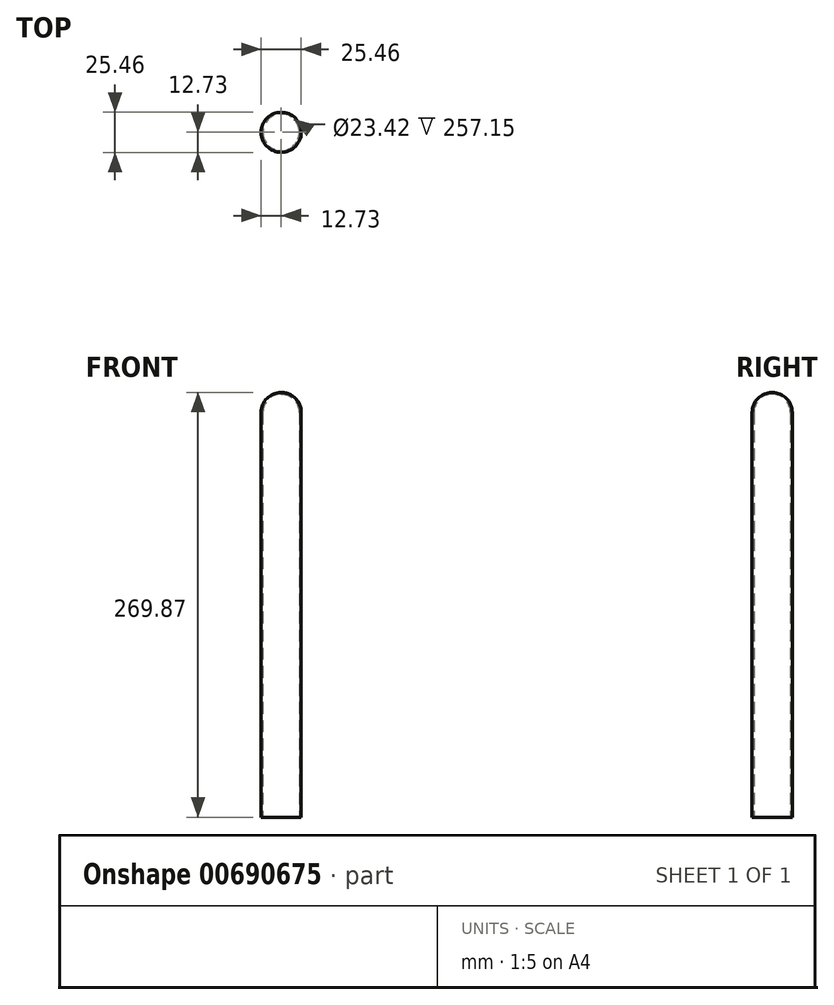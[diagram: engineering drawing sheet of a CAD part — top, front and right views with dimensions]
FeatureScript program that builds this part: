
annotation { "Feature Type Name" : "Feature", "Feature Type Description" : "" }
export const myFeature = defineFeature(function(context is Context, id is Id, definition is map)
    precondition{}
    {
        {
            var Q0;
            Q0=qCreatedBy(makeId("Front.planeOp"),FACE);
            var sketch = newSketch(context, id + "F0", { "sketchPlane" : qUnion([Q0])});
            skLineSegment(sketch, "E0", {"start": v(0, 0) * mm, "end": v(0, 269.88) * mm});
            skLineSegment(sketch, "E1", {"start": v(0, 0) * mm, "end": v(12.73, 0) * mm});
            skLineSegment(sketch, "E2", {"start": v(12.73, 0) * mm, "end": v(12.73, 257.15) * mm});
            skArc(sketch, "E3", {"start": v(12.73, 257.15) * mm, "mid": v(9, 266.15) * mm, "end": v(0, 269.88) * mm});
            skSolve(sketch);
        }
        {
            var Q0;
            Q0 = qSketchRegion(id + "F0", true);
            var Q1;
            Q1=sQuery(id+"F0.wireOp",EDGE,"E0");
            revolve(context, id + "F1", {"surfaceOperationType" : NewSurfaceOperationType.NEW, "entities" : qUnion([Q0]), "axis" : qUnion([Q1]), "revolveType" : RevolveType.FULL});
        }
        {
            var Q0;
            Q0=makeQuery(id+"F1.opRevolve","SWEPT_FACE",FACE,{"disambiguationData":[OSD([sQuery(id+"F0.wireOp",EDGE,"E1")])]});
            shell(context, id + "F2", {"entities" : qUnion([Q0]), "thickness" : 1.02 * mm});
        }
    });
